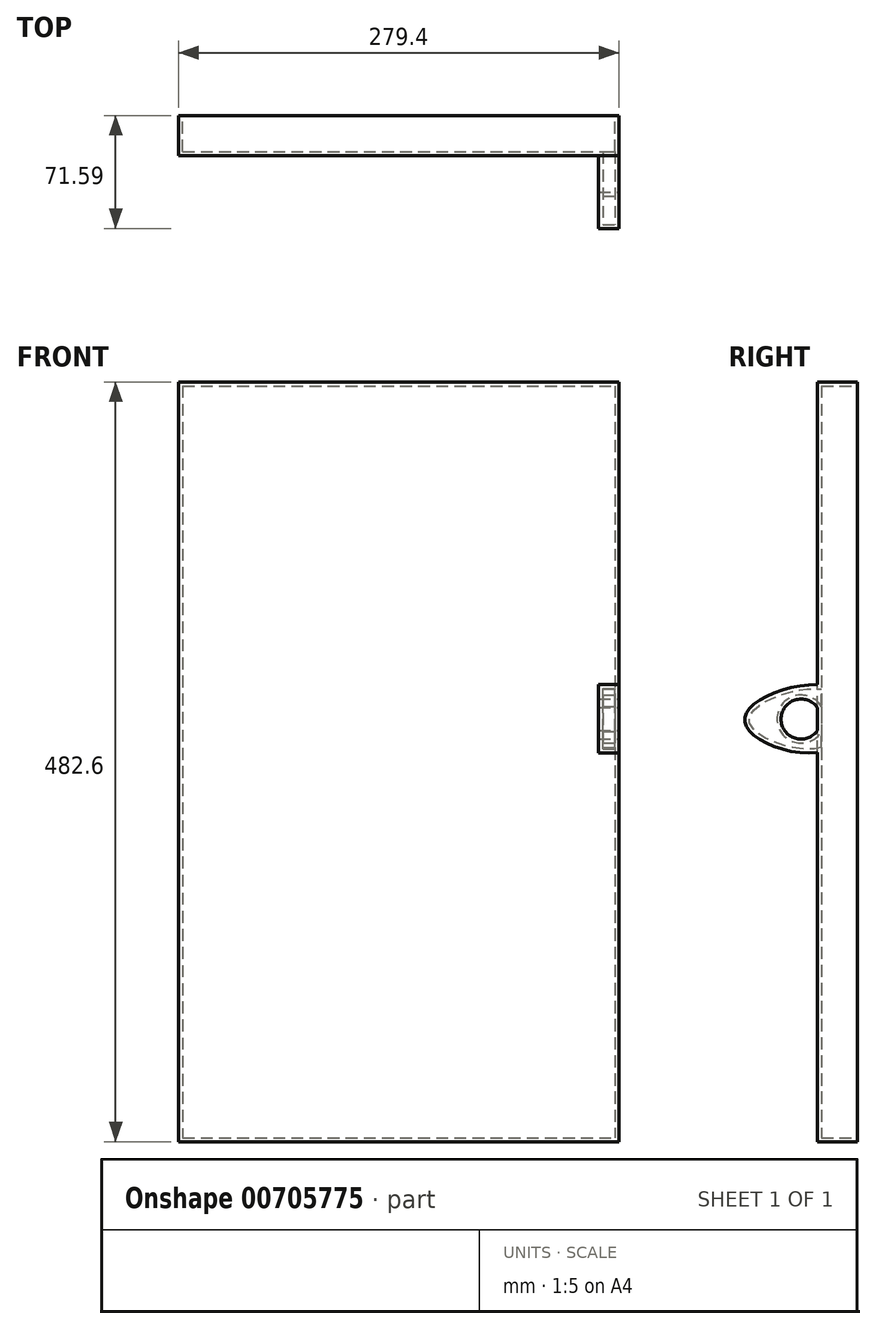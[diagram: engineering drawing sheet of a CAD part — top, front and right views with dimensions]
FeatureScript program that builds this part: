
annotation { "Feature Type Name" : "Feature", "Feature Type Description" : "" }
export const myFeature = defineFeature(function(context is Context, id is Id, definition is map)
    precondition{}
    {
        {
            var Q0;
            Q0=qCreatedBy(makeId("Front.planeOp"),FACE);
            var sketch = newSketch(context, id + "F0", { "sketchPlane" : qUnion([Q0])});
            skLineSegment(sketch, "E0.bottom", {"start": v(-139.7, 241.3) * mm, "end": v(139.7, 241.3) * mm});
            skLineSegment(sketch, "E0.top", {"start": v(-139.7, -241.3) * mm, "end": v(139.7, -241.3) * mm});
            skLineSegment(sketch, "E0.left", {"start": v(-139.7, 241.3) * mm, "end": v(-139.7, -241.3) * mm});
            skLineSegment(sketch, "E0.right", {"start": v(139.7, 241.3) * mm, "end": v(139.7, -241.3) * mm});
            skPoint(sketch, "E0.middle", {"position": v(0, 0) * mm});
            skSolve(sketch);
        }
        {
            var Q0;
            Q0=makeQuery(id+"F0.imprint","IMPRINT",FACE,{"disambiguationData":[TD([[makeQuery(id+"F0.imprint","IMPRINT",EDGE,{"derivedFrom":sQuery(id+"F0.wireOp",EDGE,"E0.bottom")}),-1.0]])]});
            extrude(context, id + "F1", {"entities" : qUnion([Q0]), "depth" : 25.4 * mm, "offsetDistance" : 25.4 * mm});
        }
        {
            var Q0;
            Q0=makeQuery(id+"F1.opExtrude","SWEPT_FACE",FACE,{"disambiguationData":[OSD([sQuery(id+"F0.wireOp",EDGE,"E0.right")])]});
            var sketch = newSketch(context, id + "F2", { "sketchPlane" : qUnion([Q0])});
            skFitSpline(sketch, "E1", {"points": [v(-12.27, 11.75) * mm, v(-55.1, 10.66) * mm, v(-71.58, 27.13) * mm, v(-52.91, 43.6) * mm, v(-11.17, 43.6) * mm, v(-12.27, 11.75) * mm]});
            skCircle(sketch, "E2", {"center": v(-35.82, 27.13) * mm, "radius": 12.7 * mm});
            skSolve(sketch);
        }
        {
            var Q0;
            {var subQ0=sQuery(id+"F2.wireOp",EDGE,"E1");var subQ1=makeQuery(id+"F1.opExtrude","CAP_EDGE",EDGE,{"disambiguationData":[OSD([sQuery(id+"F0.wireOp",EDGE,"E0.right")])],"isStart":false});var subQ2=makeQuery(id+"F2.imprint","INTERSECT",VERTEX,{"disambiguationData":[OD(0.0)],"derivedFrom":[subQ1,subQ0]});Q0=makeQuery(id+"F2.imprint","IMPRINT",FACE,{"disambiguationData":[TD([[makeQuery(id+"F2.imprint","IMPRINT",EDGE,{"disambiguationData":[TD([[subQ2,1.0]])],"derivedFrom":subQ0}),-1.0]])]});}
            var Q1;
            {var subQ0=sQuery(id+"F2.wireOp",EDGE,"E1");var subQ1=makeQuery(id+"F1.opExtrude","CAP_EDGE",EDGE,{"disambiguationData":[OSD([sQuery(id+"F0.wireOp",EDGE,"E0.right")])],"isStart":false});var subQ2=makeQuery(id+"F2.imprint","INTERSECT",VERTEX,{"disambiguationData":[OD(0.0)],"derivedFrom":[subQ1,subQ0]});Q1=makeQuery(id+"F2.imprint","IMPRINT",FACE,{"disambiguationData":[TD([[makeQuery(id+"F2.imprint","IMPRINT",EDGE,{"disambiguationData":[TD([[subQ2,-1.0]])],"derivedFrom":subQ0}),-1.0]])]});}
            extrude(context, id + "F3", {"entities" : qUnion([Q0, Q1]), "operationType" : NewBodyOperationType.ADD, "oppositeDirection" : true, "depth" : 12.7 * mm, "offsetDistance" : 25.4 * mm});
        }
        {
            var Q0;
            Q0=makeQuery(id+"F1.opExtrude","CAP_FACE",FACE,{"disambiguationData":[OSD([sQuery(id+"F0.wireOp",EDGE,"E0.bottom"),sQuery(id+"F0.wireOp",EDGE,"E0.top"),sQuery(id+"F0.wireOp",EDGE,"E0.left"),sQuery(id+"F0.wireOp",EDGE,"E0.right")])],"isStart":true});
            shell(context, id + "F4", {"entities" : qUnion([Q0]), "thickness" : 2.54 * mm});
        }
    });
